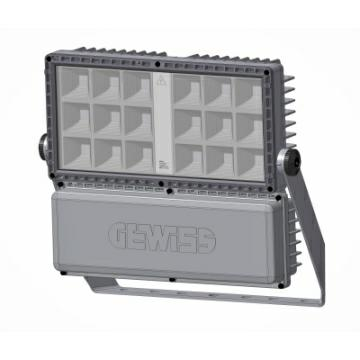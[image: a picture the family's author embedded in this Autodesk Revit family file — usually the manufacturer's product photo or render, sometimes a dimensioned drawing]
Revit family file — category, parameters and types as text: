
# Revit family: Lighting-Floodlights-GEWISS-SMART[PRO]2.0-LED-MEDIUM-POWER_1MODULE_CLI
name_source: partatom
category: Apparecchi per illuminazione
units: mm (PartAtom-declared; Revit-internal decimal feet)

## family parameters
Condiviso = No
Host = Superficie
Punto di calcolo locali = Sì
Quota connettore circolare = Usa diametro
Sorgente d'illuminazione = No
Taglio con vuoti quando caricato = No
Tipo di parte = Normale

## types (1)
- Lighting-Floodlights-GEWISS-SMART[PRO]2.0-LED-MEDIUM-POWER_1MODULE_CLI
    Applicazione = Indoor / Outdoor
    Body = Die-cast aluminium -
    Catalogue = LIGHTING
    Classification: = -
    Color Rendering Index = CRI-80
    Colour = Graphite grey
    Colour : = Polyester powder coated
    Colour temperature = 5700K
    Context = Sport, Big Areas
    Control System = Stand Alone - 1/10V
    DIN 18032-3 certification = Yes
    Descrizione = SMARTPRO2.0 1M 5700K CRI80 A3 1-10V CL1
    Device with reduced surface temperature = Yes
    Driver = Included
    Driver Box = Built-in
    Efficiency (lm/W) = 107
    Eletrical and lighting features = -
    External screw = Stainless steel
    Fixing = Bracket
    GW - Codice Electrocod = 2424
    Gasket = Anti-aging silicone
    General information = -
    Glow Wire Test : = -
    IDF = a5e66f1d-93b2-40d0-b850-0f4f564f9cc8
    IDT = e1d71c87574d4cdbb5424318827b01ba
    IP degree = IP66
    IPEA = ROAD = A // LARGE AREAS = A3 + // CYCLOPEDONALS = A + // GREEN AREAS = A + // HISTORICAL CENTER = A5 + // OTHER = A5 +
    Immagine tipo = SMARTPRO20_1M.jpg
    Installationa and maintenance = -
    Insulation class = I
    LED Maintenance = Not available
    Lifetime = L90B10 (Tq+25°C) - 50000h L90B10 (Tq+40°C) = 40000h L80B10 (Tq+25°C) - 110000h
    Locking Hook = Hexagonal metric screws
    Lumen output (lm) = 17600
    Luminaire = LED luminaire with small,mid and high lumen power
    Materials = -
    Maximum surface exposed to the wind : = 0,085 m2
    Modello = GWP2185NS
    Mouting and installation = High-mast lighting - Wall mounting - Ground mouting
    Operating temperature : = -30 +40 °C
    Optic = A3 - Assymetric Narrow
    Optic : = Polished anodised aluminum reflector with 99.99% pure aluminum
    Optic Maintenance = Not available
    Optic and illuminating features = -
    Overvoltage protection = DM 6 kV / CM 10 kV
    Photobiological Risk Class = -
    Produttore = GEWISS S.p.A.
    Prospetto di default = 1219 mm
    Rated frequency (Hz) = 50 / 60
    SEO = Floodlight
    Shield type = Flat tempered glass 4mm
    Shock resistance = IK08
    Standard Deviation Colour Matching = SDCM = 3
    Standard- = EN60598-1; EN60598-2-5; EN60598-2-24; IEC 62778; IEC62471; EN13201
    Standards and approvals = -
    Stocking temperature = -
    Supply voltage = 220 - 240 V
    System power = 165W
    Technical sheet = https://www.gewiss.com
    Tilt- = Rotation on bracket with integrated goniometer
    Type of light source = LED - Not replaceable
    URL = https://www.gewiss.com
    Unified Glare Rating = G*6 - ULOR = 0
    Unique digital code (Datamatrix) = Currently not present
    Version file RFA = 20.11
    Versions = 5700K cold light
    Warranty = 5 years
    Weight (kg): = 5,7
    Wiring = Watertight connector
